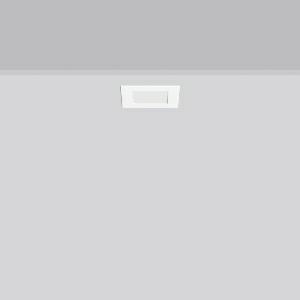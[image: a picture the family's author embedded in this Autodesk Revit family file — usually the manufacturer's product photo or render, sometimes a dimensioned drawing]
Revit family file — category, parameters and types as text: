
# Revit family: toledo_flat_square_e_901485_002_bd70
name_source: partatom
category: Lighting Fixtures
units: mm (PartAtom-declared; Revit-internal decimal feet)

## family parameters
Cut with Voids When Loaded = No
Host = Face
Light Source = No
Part Type = Normal
Room Calculation Point = No
Round Connector Dimension = Use Diameter
Shared = No

## types (1)
- TOLEDO FLAT square E (1 x LED Modul 830, 420 lm, 3000)
    Apparent Load = 5 VA
    CIE Flux Codes = 49 80 96 100 100
    Color Rendering = 80
    Color Temperature = 3000
    Default Elevation = 1800 mm
    Description = Series: TOLEDO FLAT square
Ultra thin recessed downlight. Housing: die-cast aluminium. Light guide and diffuser made of non-yellowing PMMA, opal matt. Ceiling installation with spring system. Mounting depth depends on ceiling strength. Suitable for through-wiring with separately available accessories. Surface mounted housing as accessory for all sizes. Retrofittable decorative cylinders made of chintz fabric as accessory, optional with satin finish plastic diffuser. Through-wiring box (5 pole) available as accessory. 
Colour: white
Length: 110 mm
Width: 110 mm
Height: 3 mm
Cut-out length: 96 mm
Cut-out width: 96 mm
Recess height: 27-56 mm
Luminaire: recess height: 31-51 mm
Lamp: LED
Socket: without socket
Colour temperature: 3000K
Colour rendering index (CRI): 80
System power: 5 W
Rated luminous flux: 420 lm
Luminous efficiency: 84 lm/W
Control gear: Regulated power supply
Protection class: II
Type of protection: IP 54
    Height = 0 mm  [stored 0 ft]
    Lamp = 1 x LED Modul 830
    Lamp Light Flux = 420 lm
    Lamp count = 1
    Length = 110 mm
    Lifetime = 50000 h
    Luminous efficacy = 84 lm/W
    Manufacturer = RZB
    ModVariant = No
    Model = 901485.002
    Mounting Place = Ceiling
    Mounting Type = Recessed
    Number of Poles = 1
    OnlyDefault = Yes
    Power Factor = 1
    Product Name = TOLEDO FLAT square E
    Product group = Recessed downlights
    ProductGroupID = 402
    Protection Class = Protection class II
    Protection Degree = IP 20
    RLX_Detail_Level = 1
    RLX_Emergency_Light_Flux = 0 lm
    RLX_Emergency_Type = 0
    RLX_Emergency_Type_DB = No
    RlxData = <blob elided: 57609 chars, md5=23f7292a>
    Socket = socket
    Standby Power = 0 W
    System Light Flux = 420 lm
    System Power = 5 W
    Type Comments = Product without accessories
    Type Image = 901485.002.jpg
    URL = http://relux.com
    VarID = ---
    Voltage = 230 V
    Voltage Range = 220-240 V
    Weight = 0.00 kg
    Width = 110 mm

note: [stored X ft] marks values corroborated as IEEE doubles in the binary element streams (Revit-internal decimal feet)

## geometry (parser evidence)
native form markers: Blend x4, Sweep x10
no freeform markers — native parametric forms only
